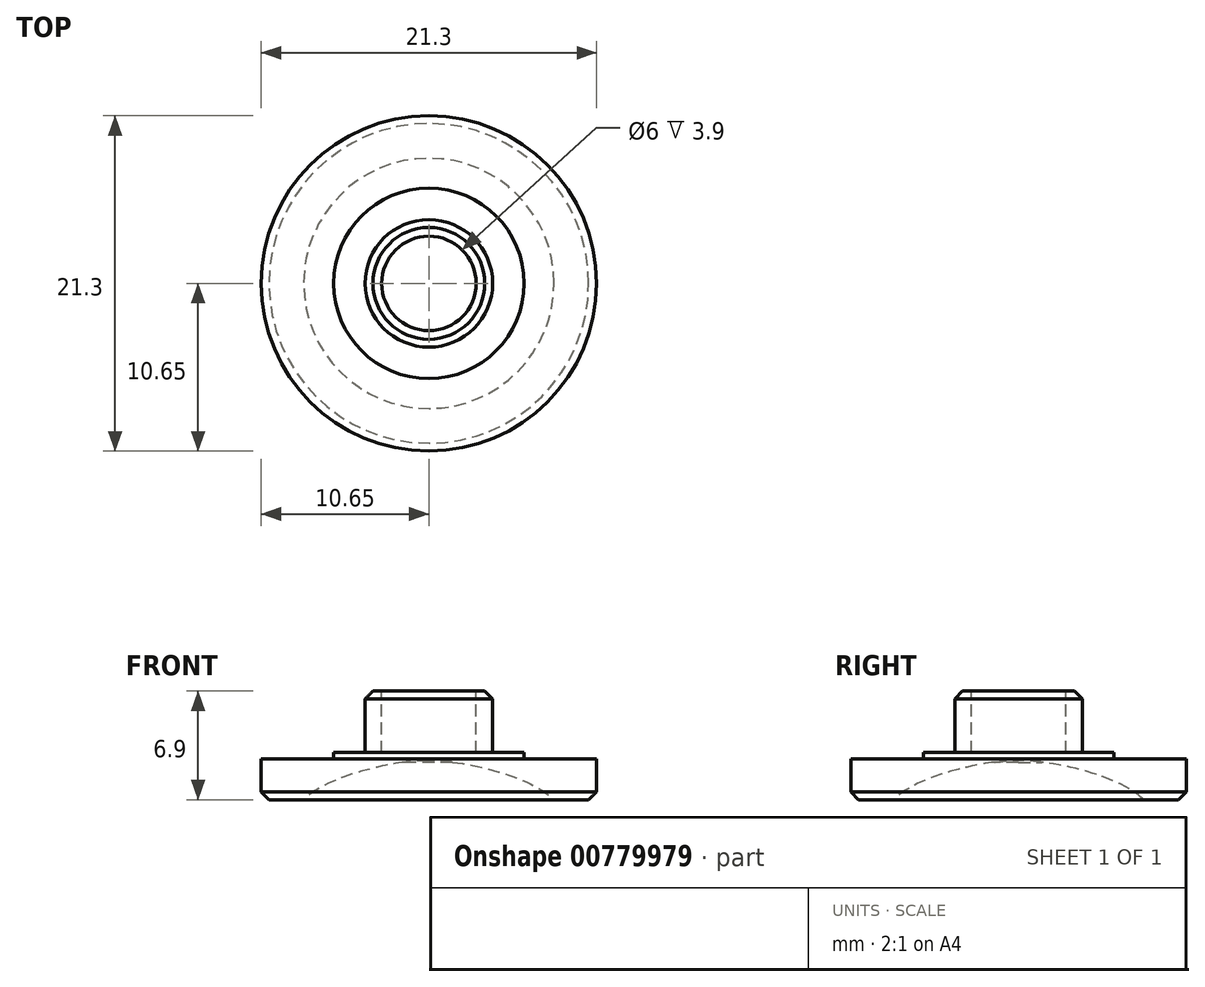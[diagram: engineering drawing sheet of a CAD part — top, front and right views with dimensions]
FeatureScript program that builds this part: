
annotation { "Feature Type Name" : "Feature", "Feature Type Description" : "" }
export const myFeature = defineFeature(function(context is Context, id is Id, definition is map)
    precondition{}
    {
        {
            var Q0;
            Q0=qCreatedBy(makeId("Front.planeOp"),FACE);
            var sketch = newSketch(context, id + "F0", { "sketchPlane" : qUnion([Q0])});
            skLineSegment(sketch, "E0", {"start": v(0, 0) * mm, "end": v(7.95, 0) * mm});
            skLineSegment(sketch, "E1", {"start": v(7.95, 0) * mm, "end": v(10.65, 0) * mm});
            skLineSegment(sketch, "E2", {"start": v(10.65, 0) * mm, "end": v(10.65, 2.6) * mm});
            skLineSegment(sketch, "E3", {"start": v(10.65, 2.6) * mm, "end": v(6.05, 2.6) * mm});
            skLineSegment(sketch, "E4", {"start": v(6.05, 2.6) * mm, "end": v(6.05, 3) * mm});
            skLineSegment(sketch, "E5", {"start": v(6.05, 3) * mm, "end": v(4.05, 3) * mm});
            skLineSegment(sketch, "E6", {"start": v(4.05, 3) * mm, "end": v(4.05, 6.9) * mm});
            skLineSegment(sketch, "E7", {"start": v(4.05, 6.9) * mm, "end": v(0, 6.9) * mm});
            skLineSegment(sketch, "E8", {"start": v(0, 6.9) * mm, "end": v(0, 0) * mm});
            skLineSegment(sketch, "E9", {"start": v(0, 0) * mm, "end": v(0, 2.5) * mm});
            skFitSpline(sketch, "E10", {"points": [v(0, 2.5) * mm, v(7.95, 0) * mm], "startDerivative": vector(7.15, -0.05) * mm, "endDerivative": vector(4.23, -4.42) * mm});
            skLineSegment(sketch, "E11", {"start": v(0, 2.89) * mm, "end": v(1.5, 2.89) * mm});
            skLineSegment(sketch, "E12", {"start": v(1.5, 2.89) * mm, "end": v(1.5, 2.39) * mm});
            skSolve(sketch);
        }
        {
            var Q0;
            Q0=makeQuery(id+"F0.imprint","IMPRINT",FACE,{"disambiguationData":[TD([[makeQuery(id+"F0.imprint","IMPRINT",EDGE,{"derivedFrom":sQuery(id+"F0.wireOp",EDGE,"E1")}),1.0]])]});
            var Q1;
            {var subQ3=sQuery(id+"F0.wireOp",EDGE,"E11");Q1=makeQuery(id+"F0.imprint","IMPRINT",FACE,{"disambiguationData":[TD([[makeQuery(id+"F0.imprint","IMPRINT",EDGE,{"derivedFrom":subQ3}),-1.0]])]});}
            var Q2;
            Q2=sQuery(id+"F0.wireOp",EDGE,"E8");
            revolve(context, id + "F1", {"surfaceOperationType" : NewSurfaceOperationType.NEW, "entities" : qUnion([Q0, Q1]), "axis" : qUnion([Q2]), "revolveType" : RevolveType.FULL});
        }
        {
            var Q0;
            Q0=makeQuery(id+"F1.opRevolve","SWEPT_EDGE",EDGE,{"disambiguationData":[OSD([sQuery(id+"F0.wireOp",EDGE,"E6"),sQuery(id+"F0.wireOp",EDGE,"E7")])]});
            chamfer(context, id + "F2", {"entities" : qUnion([Q0]), "width" : .5 * mm, "tangentPropagation" : true});
        }
        {
            var Q0;
            Q0=makeQuery(id+"F1.opRevolve","SWEPT_EDGE",EDGE,{"disambiguationData":[OSD([sQuery(id+"F0.wireOp",EDGE,"E1"),sQuery(id+"F0.wireOp",EDGE,"E2")])]});
            chamfer(context, id + "F3", {"entities" : qUnion([Q0]), "width" : .5 * mm, "tangentPropagation" : true});
        }
        {
            var Q0;
            Q0=qCreatedBy(makeId("Top.planeOp"),FACE);
            cPlane(context, id + "F4", {"entities" : qUnion([Q0]), "cplaneType" : CPlaneType.OFFSET, "offset" : 6.9 * mm, "width" : 150 * mm, "height" : 150 * mm});
        }
        {
            var Q0;
            Q0=qCreatedBy(id+"F4.planeOp",FACE);
            var sketch = newSketch(context, id + "F5", { "sketchPlane" : qUnion([Q0])});
            skCircle(sketch, "E13", {"center": v(0, 0) * mm, "radius": 3 * mm});
            skLineSegment(sketch, "E14", {"start": v(0, 0) * mm, "end": v(0.3, 0) * mm});
            skLineSegment(sketch, "E15", {"start": v(0, 0) * mm, "end": v(-0.3, 0) * mm});
            skLineSegment(sketch, "E16", {"start": v(0.3, 0) * mm, "end": v(0.3, -4.24) * mm});
            skLineSegment(sketch, "E17", {"start": v(0.3, 0) * mm, "end": v(0.3, 4.03) * mm});
            skLineSegment(sketch, "E18.bottom", {"start": v(-0.3, 0) * mm, "end": v(0.3, 0) * mm});
            skLineSegment(sketch, "E18.left", {"start": v(-0.3, 0) * mm, "end": v(-0.3, 4.03) * mm});
            skLineSegment(sketch, "E19.left", {"start": v(-0.3, 0) * mm, "end": v(-0.3, -4.24) * mm});
            skSolve(sketch);
        }
        {
            var Q0;
            Q0=qSketchRegion(id+"F5",true);
            extrude(context, id + "F6", {"entities" : qUnion([Q0]), "operationType" : NewBodyOperationType.REMOVE, "oppositeDirection" : true, "depth" : 3.9 * mm, "offsetDistance" : 25 * mm});
        }
    });
